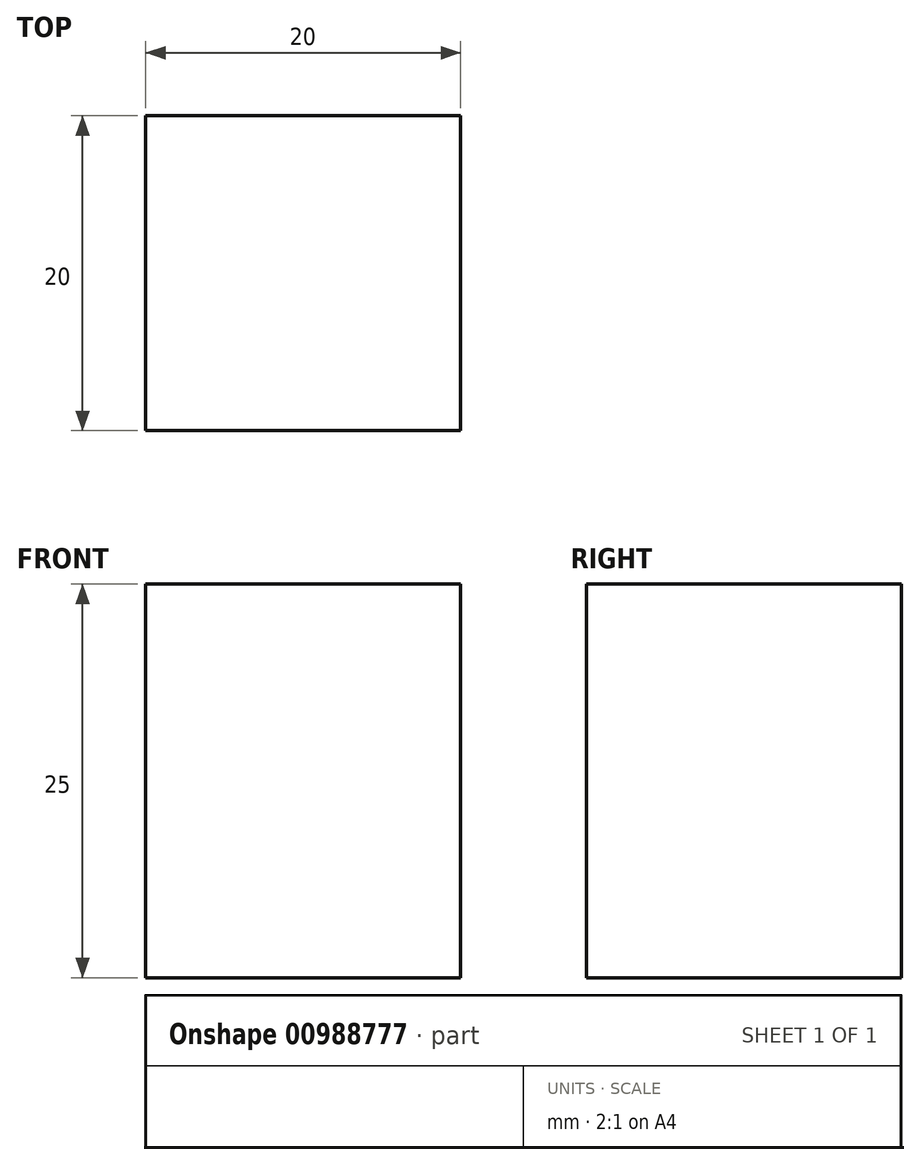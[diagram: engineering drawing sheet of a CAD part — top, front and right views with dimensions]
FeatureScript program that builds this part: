
annotation { "Feature Type Name" : "Feature", "Feature Type Description" : "" }
export const myFeature = defineFeature(function(context is Context, id is Id, definition is map)
    precondition{}
    {
        {
            var Q0;
            Q0=qCreatedBy(makeId("Top.planeOp"),FACE);
            var sketch = newSketch(context, id + "F0", { "sketchPlane" : qUnion([Q0])});
            skLineSegment(sketch, "E0.bottom", {"start": v(-20, -20) * mm, "end": v(0, -20) * mm});
            skLineSegment(sketch, "E0.top", {"start": v(-20, 0) * mm, "end": v(0, 0) * mm});
            skLineSegment(sketch, "E0.left", {"start": v(-20, -20) * mm, "end": v(-20, 0) * mm});
            skLineSegment(sketch, "E0.right", {"start": v(0, -20) * mm, "end": v(0, 0) * mm});
            skSolve(sketch);
        }
        {
            var Q0;
            Q0=makeQuery(id+"F0.imprint","IMPRINT",FACE,{"disambiguationData":[TD([[makeQuery(id+"F0.imprint","IMPRINT",EDGE,{"derivedFrom":sQuery(id+"F0.wireOp",EDGE,"E0.bottom")}),1.0]])]});
            extrude(context, id + "F1", {"entities" : qUnion([Q0]), "depth" : 25 * mm, "offsetDistance" : 25 * mm});
        }
    });
